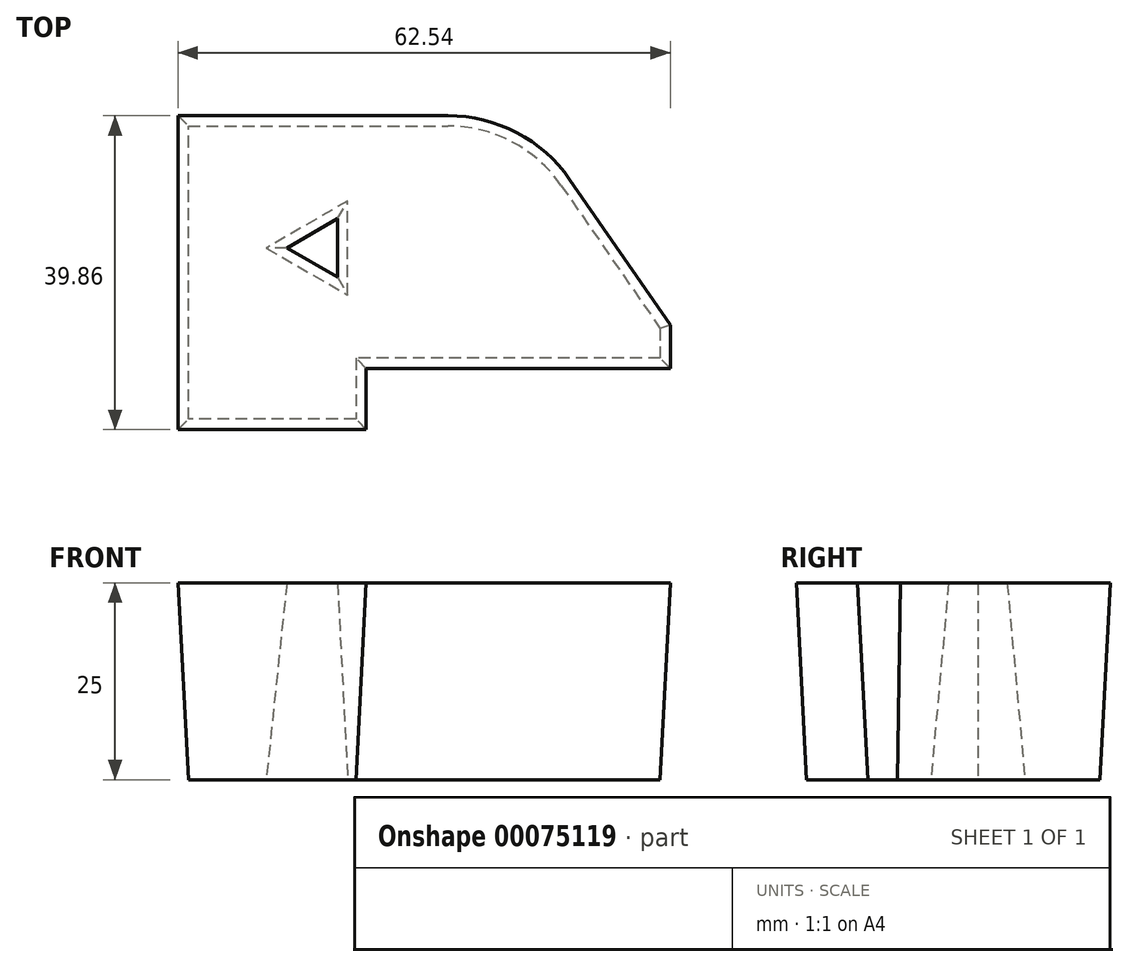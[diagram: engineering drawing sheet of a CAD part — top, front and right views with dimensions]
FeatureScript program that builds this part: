
annotation { "Feature Type Name" : "Feature", "Feature Type Description" : "" }
export const myFeature = defineFeature(function(context is Context, id is Id, definition is map)
    precondition{}
    {
        {
            var Q0;
            Q0=qCreatedBy(makeId("Top.planeOp"),FACE);
            var sketch = newSketch(context, id + "F0", { "sketchPlane" : qUnion([Q0])});
            skLineSegment(sketch, "E0", {"start": v(0, 0) * mm, "end": v(0, 37.24) * mm});
            skLineSegment(sketch, "E1", {"start": v(0, 37.24) * mm, "end": v(32.97, 37.24) * mm});
            skArc(sketch, "E2", {"start": v(32.97, 37.24) * mm, "mid": v(41.1, 35.24) * mm, "end": v(47.36, 29.7) * mm});
            skLineSegment(sketch, "E3", {"start": v(47.36, 29.7) * mm, "end": v(59.92, 11.52) * mm});
            skLineSegment(sketch, "E4", {"start": v(59.92, 11.52) * mm, "end": v(59.92, 7.77) * mm});
            skLineSegment(sketch, "E5", {"start": v(59.92, 7.77) * mm, "end": v(21.28, 7.77) * mm});
            skLineSegment(sketch, "E6", {"start": v(21.28, 7.77) * mm, "end": v(21.28, 0) * mm});
            skLineSegment(sketch, "E7", {"start": v(21.28, 0) * mm, "end": v(0, 0) * mm});
            skCircle(sketch, "E8.cCircle", {"center": v(16.8, 21.75) * mm, "radius": 3.45 * mm, "construction": true});
            skLineSegment(sketch, "E8.0", {"start": v(20.25, 27.74) * mm, "end": v(20.25, 15.77) * mm});
            skLineSegment(sketch, "E8.1", {"start": v(20.25, 15.77) * mm, "end": v(9.89, 21.75) * mm});
            skLineSegment(sketch, "E8.2", {"start": v(9.89, 21.75) * mm, "end": v(20.25, 27.74) * mm});
            skPoint(sketch, "E8.0.midPoint", {"position": v(20.25, 21.75) * mm});
            skSolve(sketch);
        }
        {
            var Q0;
            Q0 = qSketchRegion(id + "F0", true);
            extrude(context, id + "F1", {"entities" : qUnion([Q0]), "depth" : 25 * mm, "hasDraft" : true, "draftAngle" : 3 * degree});
        }
    });
